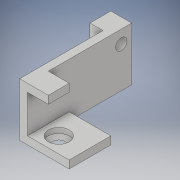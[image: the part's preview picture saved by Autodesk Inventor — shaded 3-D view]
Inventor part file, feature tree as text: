
AUTODESK INVENTOR PART (.ipt)
format: ipt  version: 2017 (Build 210142000, 142)  size: 153,600 bytes
history: native  units: in
note: dims shown in document units (in); Inventor stores cm internally (conversion verified against a paired STEP export)
features: sketch x6, projected_geometry x6, extrude x4, hole x2
ambient origin geometry x8: Origin, YZ Plane, XZ Plane, XY Plane, X Axis, Y Axis, Z Axis, Center Point
bodies: Solid1 (feature_tree)
feature tree (18):
  extrude  "Extrusion1"  Depth=2.5in
  extrude  "Extrusion2"  Depth=0.5in
  extrude  "Extrusion3"  Depth=0.5in TaperAngle=0.0deg
  extrude  "Extrusion4"  Depth=1.0in TaperAngle=0.0deg
  hole  "Hole1"  [1 undecoded]
  hole  "Hole2"  [1 undecoded]
  sketch  "Sketch1"  dims[d0=1.2813in d1=2.5in]
  sketch  "Sketch2"  dims[d2=0.1875in d3=0.0in d4=0.5in]
  projected_geometry  "Projected Loop1"
  sketch  "Sketch3"  dims[d5=0.1875in d6=0.5in d7=0.0in]
  projected_geometry  "Projected Loop2"
  sketch  "Sketch4"  dims[d8=0.1875in d9=1.0in d10=0.0in]
  projected_geometry  "Projected Loop3"
  sketch  "Sketch5"  dims[d11=0.5in d12=0.625in]
  projected_geometry  "Projected Loop4"
  projected_geometry  "Projected Loop5"
  sketch  "Sketch6"  dims[d13=0.3125in d14=0.0in d15=0.1875in d16=0.3125in d17=0.25in d18=0.27in d19=0.75in d20=0.375in d21=0.25in d22=0.5635in d23=1.0in d24=0.8108in d25=0.375in d26=0.375in d27=0.5in d28=0.75in d29=0.375in d30=0.25in d31=0.5635in d32=0.125in d33=0.8108in]
  projected_geometry  "Projected Loop6"
note: 2 required parameter values undecoded (feature->parameter linkage not recoverable at this tier; creation-order binding heuristic only, values carry confidence <= 0.55)
